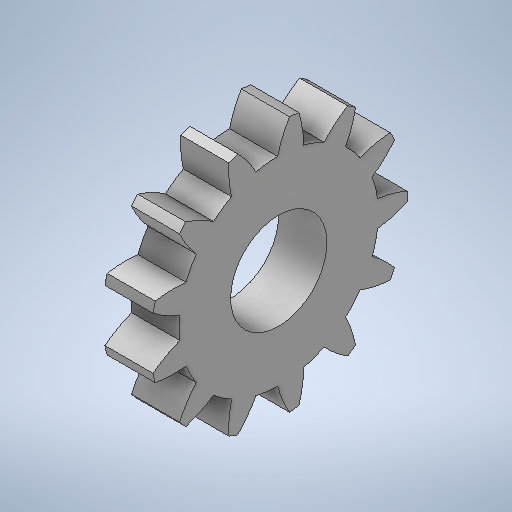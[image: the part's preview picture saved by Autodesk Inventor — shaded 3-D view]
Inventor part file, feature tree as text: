
AUTODESK INVENTOR PART (.ipt)
format: ipt  version: 2025.2 (Build 292293000, 293)  size: 324,096 bytes
history: native  units: in
note: dims shown in document units (in); Inventor stores cm internally (conversion verified against a paired STEP export)
features: other x4, extrude x1, pattern_circular x1
ambient origin geometry x8: Origin, YZ Plane, XZ Plane, XY Plane, X Axis, Y Axis, Z Axis, Center Point
bodies: Volumenkörper1 (feature_tree)
feature tree (6):
  other  "Skelett_Laufkatze.ipt"
  other  "Rohling_Zahnrad"
  extrude  "Zahngeometrie"  Depth=0.3937in
  pattern_circular  "Anzahl_zähne"  Angle=90.0deg  [1 undecoded]
  other  "Zahnrad_Zahnrad_seite"
  other  "Zahnrad_Zahnrad_front"
note: 1 required parameter value undecoded (feature->parameter linkage not recoverable at this tier; creation-order binding heuristic only, values carry confidence <= 0.55)
